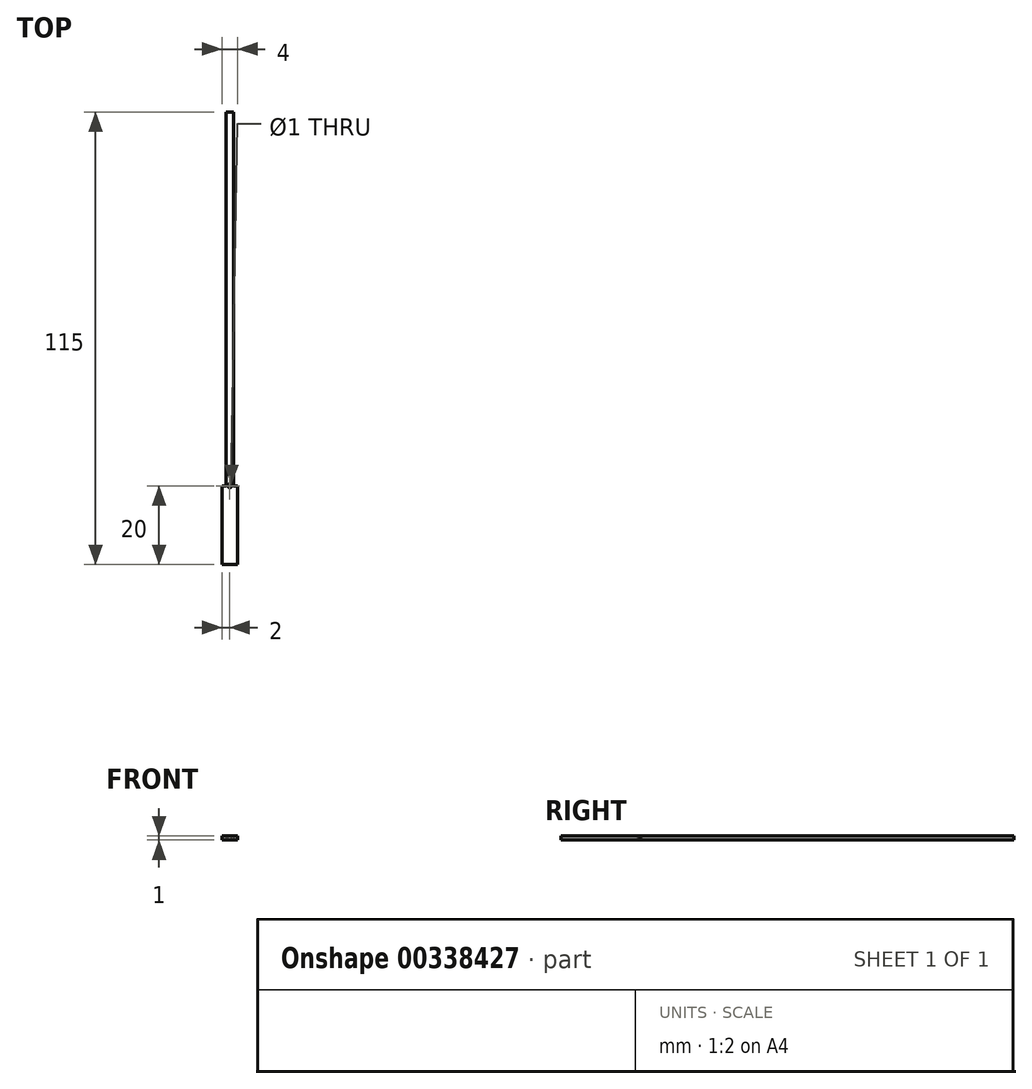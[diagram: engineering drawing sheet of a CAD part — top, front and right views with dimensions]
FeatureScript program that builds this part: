
annotation { "Feature Type Name" : "Feature", "Feature Type Description" : "" }
export const myFeature = defineFeature(function(context is Context, id is Id, definition is map)
    precondition{}
    {
        {
            var Q0;
            Q0=qCreatedBy(makeId("Top.planeOp"),FACE);
            var sketch = newSketch(context, id + "F0", { "sketchPlane" : qUnion([Q0])});
            skCircle(sketch, "E0", {"center": v(0, 0) * mm, "radius": 105 * mm, "construction": true});
            skCircle(sketch, "E1", {"center": v(0, 0) * mm, "radius": 125 * mm, "construction": true});
            skLineSegment(sketch, "E2.top", {"start": v(-1, 95) * mm, "end": v(1, 95) * mm});
            skLineSegment(sketch, "E2.left", {"start": v(-1, 0) * mm, "end": v(-1, 95) * mm});
            skLineSegment(sketch, "E2.right", {"start": v(1, 0) * mm, "end": v(1, 95) * mm});
            skLineSegment(sketch, "E3.bottom", {"start": v(-2, -20) * mm, "end": v(2, -20) * mm});
            skLineSegment(sketch, "E3.top", {"start": v(-2, 0) * mm, "end": v(-1, 0) * mm});
            skLineSegment(sketch, "E3.left", {"start": v(-2, -20) * mm, "end": v(-2, 0) * mm});
            skLineSegment(sketch, "E3.right", {"start": v(2, -20) * mm, "end": v(2, 0) * mm});
            skLineSegment(sketch, "E4.trimOffspring", {"start": v(1, 0) * mm, "end": v(2, 0) * mm});
            skLineSegment(sketch, "E5", {"start": v(-1, 0) * mm, "end": v(0, 0) * mm, "construction": true});
            skLineSegment(sketch, "E6", {"start": v(0, 0) * mm, "end": v(1, 0) * mm, "construction": true});
            skSolve(sketch);
        }
        {
            var Q0;
            Q0 = qSketchRegion(id + "F0", true);
            extrude(context, id + "F1", {"entities" : qUnion([Q0]), "depth" : 1 * mm});
        }
        {
            var Q0;
            Q0=makeQuery(id+"F1.opExtrude","CAP_FACE",FACE,{"disambiguationData":[OSD([sQuery(id+"F0.wireOp",EDGE,"E2.top"),sQuery(id+"F0.wireOp",EDGE,"E2.left"),sQuery(id+"F0.wireOp",EDGE,"E2.right"),sQuery(id+"F0.wireOp",EDGE,"E3.bottom"),sQuery(id+"F0.wireOp",EDGE,"E3.top"),sQuery(id+"F0.wireOp",EDGE,"E3.left"),sQuery(id+"F0.wireOp",EDGE,"E3.right"),sQuery(id+"F0.wireOp",EDGE,"E4.trimOffspring")])],"isStart":false});
            var sketch = newSketch(context, id + "F2", { "sketchPlane" : qUnion([Q0])});
            skCircle(sketch, "E7", {"center": v(0, 0) * mm, "radius": 0.5 * mm});
            skSolve(sketch);
        }
        {
            var Q0;
            Q0=makeQuery(id+"F2.imprint","IMPRINT",FACE,{"disambiguationData":[TD([[makeQuery(id+"F2.imprint","IMPRINT",EDGE,{"derivedFrom":sQuery(id+"F2.wireOp",EDGE,"E7")}),1.0]])]});
            extrude(context, id + "F3", {"entities" : qUnion([Q0]), "operationType" : NewBodyOperationType.REMOVE, "endBound" : BoundingType.THROUGH_ALL, "oppositeDirection" : true, "depth" : 25 * mm});
        }
    });
